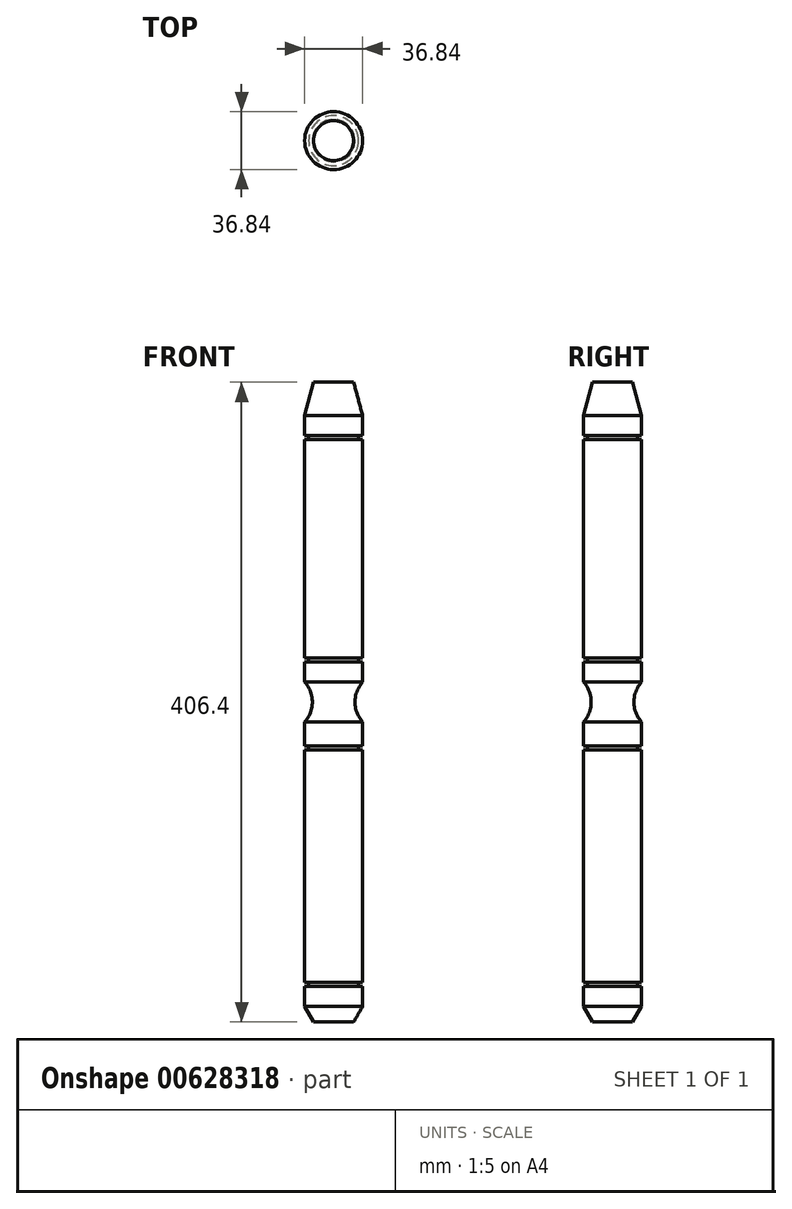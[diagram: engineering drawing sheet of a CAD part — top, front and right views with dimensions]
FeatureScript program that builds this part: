
annotation { "Feature Type Name" : "Feature", "Feature Type Description" : "" }
export const myFeature = defineFeature(function(context is Context, id is Id, definition is map)
    precondition{}
    {
        {
            var Q0;
            Q0=qCreatedBy(makeId("Front.planeOp"),FACE);
            var sketch = newSketch(context, id + "F0", { "sketchPlane" : qUnion([Q0])});
            skLineSegment(sketch, "E0", {"start": v(0, 203.2) * mm, "end": v(0, -203.2) * mm});
            skLineSegment(sketch, "E1", {"start": v(0, -203.2) * mm, "end": v(12.7, -203.2) * mm});
            skLineSegment(sketch, "E2", {"start": v(12.7, -203.2) * mm, "end": v(18.41, -193.3) * mm});
            skLineSegment(sketch, "E3", {"start": v(18.41, -193.3) * mm, "end": v(18.41, -180.6) * mm});
            skLineSegment(sketch, "E4", {"start": v(0, 203.2) * mm, "end": v(12.7, 203.2) * mm});
            skLineSegment(sketch, "E5", {"start": v(12.7, 203.2) * mm, "end": v(18.41, 181.87) * mm});
            skLineSegment(sketch, "E6", {"start": v(18.42, 181.87) * mm, "end": v(18.42, 169.17) * mm});
            skArc(sketch, "E7", {"start": v(18.41, 12.7) * mm, "mid": v(13.56, 0) * mm, "end": v(18.42, -12.7) * mm});
            skPoint(sketch, "E8.positionSnap0", {"position": v(13.56, 0) * mm});
            skPoint(sketch, "E9", {"position": v(0, 0) * mm});
            skLineSegment(sketch, "E10", {"start": v(18.41, 169.17) * mm, "end": v(15.87, 169.17) * mm});
            skLineSegment(sketch, "E11", {"start": v(15.87, 169.17) * mm, "end": v(15.87, 166.63) * mm});
            skLineSegment(sketch, "E12", {"start": v(15.87, 166.63) * mm, "end": v(18.41, 166.63) * mm});
            skLineSegment(sketch, "E13.trimOffspring", {"start": v(18.42, 166.63) * mm, "end": v(18.41, 27.94) * mm});
            skLineSegment(sketch, "E14", {"start": v(18.42, -27.94) * mm, "end": v(15.87, -27.94) * mm});
            skLineSegment(sketch, "E15", {"start": v(15.88, -27.94) * mm, "end": v(15.88, -30.48) * mm});
            skLineSegment(sketch, "E16", {"start": v(15.88, -30.48) * mm, "end": v(18.42, -30.48) * mm});
            skLineSegment(sketch, "E17.trimOffspring", {"start": v(18.42, -12.7) * mm, "end": v(18.42, -27.94) * mm});
            skLineSegment(sketch, "E18", {"start": v(18.41, 27.94) * mm, "end": v(15.87, 27.94) * mm});
            skLineSegment(sketch, "E19", {"start": v(15.88, 27.94) * mm, "end": v(15.88, 25.4) * mm});
            skLineSegment(sketch, "E20", {"start": v(15.88, 25.4) * mm, "end": v(18.42, 25.4) * mm});
            skLineSegment(sketch, "E21.trimOffspring", {"start": v(18.41, 12.7) * mm, "end": v(18.41, 25.4) * mm});
            skLineSegment(sketch, "E22", {"start": v(18.42, -178.06) * mm, "end": v(15.88, -178.06) * mm});
            skLineSegment(sketch, "E23", {"start": v(15.88, -178.06) * mm, "end": v(15.88, -180.6) * mm});
            skLineSegment(sketch, "E24", {"start": v(15.88, -180.6) * mm, "end": v(18.41, -180.6) * mm});
            skLineSegment(sketch, "E25.trimOffspring", {"start": v(18.41, -178.06) * mm, "end": v(18.41, -30.48) * mm});
            skLineSegment(sketch, "E26.trimOffspring", {"start": v(18.41, -12.7) * mm, "end": v(18.41, -27.94) * mm});
            skLineSegment(sketch, "E27.trimOffspring", {"start": v(18.41, -27.94) * mm, "end": v(18.41, -12.7) * mm});
            skLineSegment(sketch, "E28.trimOffspring", {"start": v(18.41, 25.4) * mm, "end": v(18.41, 12.7) * mm});
            skSolve(sketch);
        }
        {
            var Q0;
            Q0=makeQuery(id+"F0.imprint","IMPRINT",FACE,{"disambiguationData":[TD([[makeQuery(id+"F0.imprint","IMPRINT",EDGE,{"derivedFrom":sQuery(id+"F0.wireOp",EDGE,"E0")}),1.0]])]});
            var Q1;
            Q1=sQuery(id+"F0.wireOp",EDGE,"E0");
            revolve(context, id + "F1", {"entities" : qUnion([Q0]), "axis" : qUnion([Q1]), "revolveType" : RevolveType.FULL});
        }
    });
